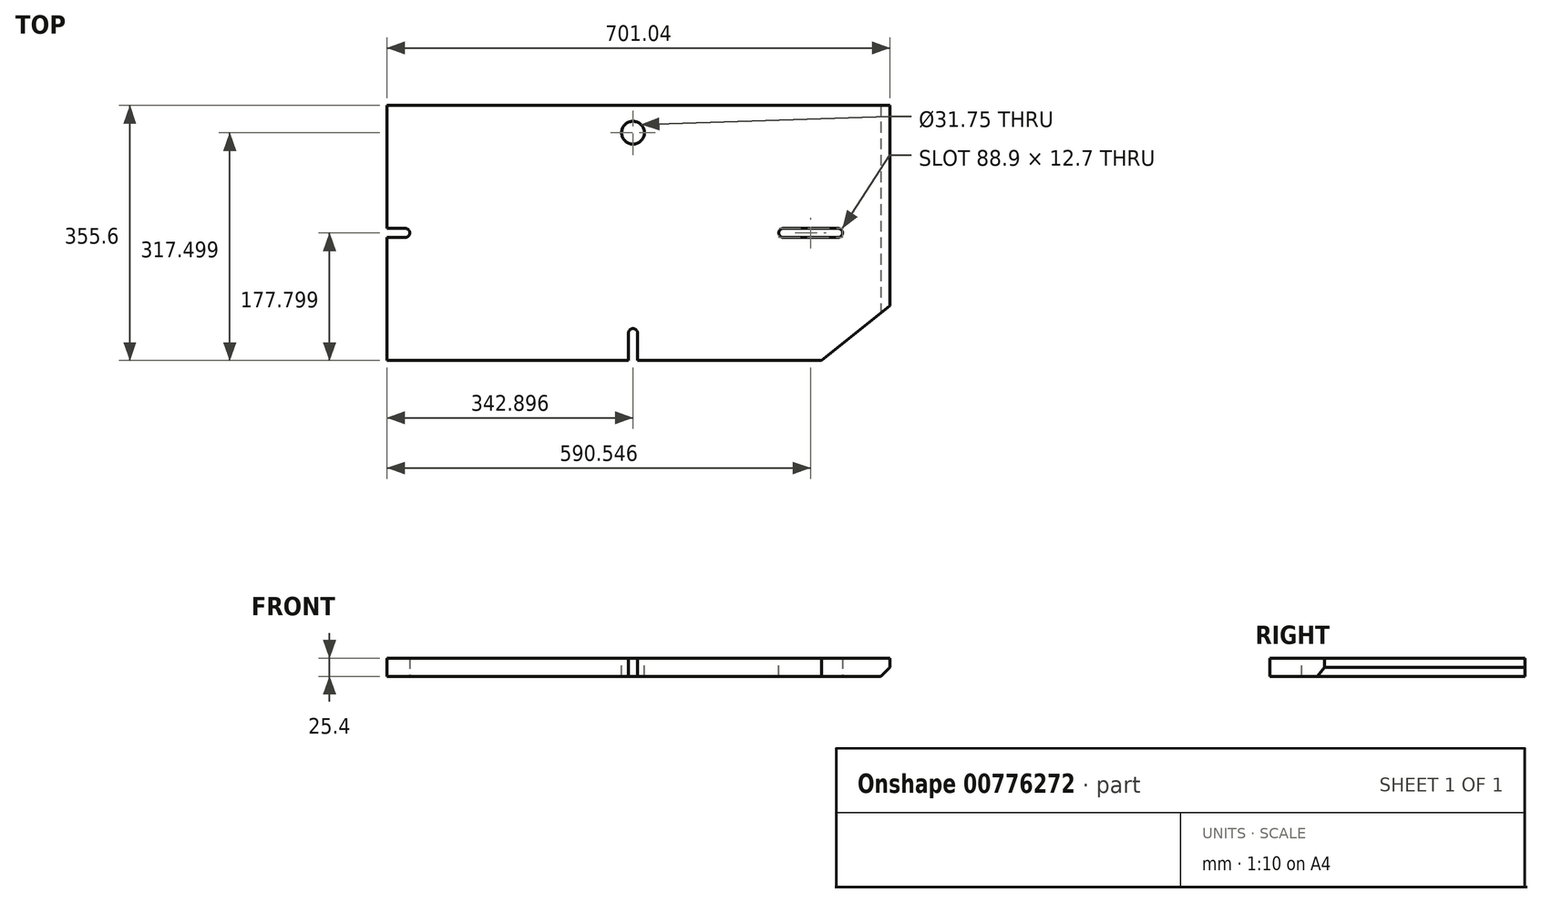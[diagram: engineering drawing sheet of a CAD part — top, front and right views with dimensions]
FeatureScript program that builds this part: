
annotation { "Feature Type Name" : "Feature", "Feature Type Description" : "" }
export const myFeature = defineFeature(function(context is Context, id is Id, definition is map)
    precondition{}
    {
        {
            var Q0;
            Q0=qCreatedBy(makeId("Top.planeOp"),FACE);
            var sketch = newSketch(context, id + "F0", { "sketchPlane" : qUnion([Q0])});
            skLineSegment(sketch, "E0.bottom", {"start": v(-409.1, 222.86) * mm, "end": v(-49.42, 222.86) * mm});
            skLineSegment(sketch, "E0.top", {"start": v(-409.1, -132.74) * mm, "end": v(196.69, -132.74) * mm});
            skLineSegment(sketch, "E0.left", {"start": v(-409.1, 222.86) * mm, "end": v(-409.1, 57.75) * mm});
            skLineSegment(sketch, "E0.right", {"start": v(291.94, 222.86) * mm, "end": v(291.94, -56.54) * mm});
            skLineSegment(sketch, "E1", {"start": v(196.69, -132.74) * mm, "end": v(291.94, -56.54) * mm});
            skLineSegment(sketch, "E2.trimOffspring", {"start": v(-409.1, 32.4) * mm, "end": v(-409.1, -132.74) * mm});
            skLineSegment(sketch, "E3.trimOffspring", {"start": v(-50.96, 222.86) * mm, "end": v(291.94, 222.86) * mm});
            skLineSegment(sketch, "E4", {"start": v(-409.1, 57.75) * mm, "end": v(-409.1, 32.4) * mm});
            skSolve(sketch);
        }
        {
            var Q0;
            Q0 = qSketchRegion(id + "F0", true);
            extrude(context, id + "F1", {"entities" : qUnion([Q0]), "depth" : 25.4 * mm, "offsetDistance" : 25.4 * mm});
        }
        {
            var Q0;
            Q0=makeQuery(id+"F1.opExtrude","CAP_FACE",FACE,{"disambiguationData":[OSD([sQuery(id+"F0.wireOp",EDGE,"E0.bottom"),sQuery(id+"F0.wireOp",EDGE,"E0.top"),sQuery(id+"F0.wireOp",EDGE,"E0.left"),sQuery(id+"F0.wireOp",EDGE,"E0.right"),sQuery(id+"F0.wireOp",EDGE,"E1"),sQuery(id+"F0.wireOp",EDGE,"E2.trimOffspring"),sQuery(id+"F0.wireOp",EDGE,"E3.trimOffspring"),sQuery(id+"F0.wireOp",EDGE,"E4")])],"isStart":false});
            var sketch = newSketch(context, id + "F2", { "sketchPlane" : qUnion([Q0])});
            skLineSegment(sketch, "E5.bottom", {"start": v(-409.1, 51.4) * mm, "end": v(-377.35, 51.4) * mm});
            skLineSegment(sketch, "E5.top", {"start": v(-409.1, 38.7) * mm, "end": v(-377.35, 38.7) * mm});
            skLineSegment(sketch, "E5.left", {"start": v(-409.1, 51.4) * mm, "end": v(-409.1, 38.7) * mm});
            skLineSegment(sketch, "E5.right", {"start": v(-377.35, 51.4) * mm, "end": v(-377.35, 38.7) * mm});
            skLineSegment(sketch, "E6.bottom", {"start": v(137, 51.4) * mm, "end": v(225.9, 51.4) * mm});
            skLineSegment(sketch, "E6.top", {"start": v(137, 38.7) * mm, "end": v(225.9, 38.7) * mm});
            skLineSegment(sketch, "E6.left", {"start": v(137, 51.4) * mm, "end": v(137, 38.7) * mm});
            skLineSegment(sketch, "E6.right", {"start": v(225.9, 51.4) * mm, "end": v(225.9, 38.7) * mm});
            skArc(sketch, "E7", {"start": v(-59.85, -94.64) * mm, "mid": v(-66.2, -88.3) * mm, "end": v(-72.55, -94.64) * mm});
            skLineSegment(sketch, "E8", {"start": v(-72.55, -94.64) * mm, "end": v(-72.55, -137.45) * mm});
            skLineSegment(sketch, "E9", {"start": v(-59.85, -94.64) * mm, "end": v(-59.85, -142.53) * mm});
            skLineSegment(sketch, "E10", {"start": v(-72.55, -137.45) * mm, "end": v(-59.85, -142.53) * mm});
            skCircle(sketch, "E11", {"center": v(-66.2, 184.76) * mm, "radius": 15.88 * mm});
            skSolve(sketch);
        }
        {
            var Q0;
            Q0 = qSketchRegion(id + "F2", true);
            extrude(context, id + "F3", {"entities" : qUnion([Q0]), "operationType" : NewBodyOperationType.REMOVE, "endBound" : BoundingType.THROUGH_ALL, "oppositeDirection" : true, "depth" : 25.4 * mm, "offsetDistance" : 25.4 * mm});
        }
        {
            var Q0;
            Q0=makeQuery(id+"F3.boolean.opBoolean","COPY",EDGE,{"derivedFrom":makeQuery(id+"F3.opExtrude","SWEPT_EDGE",EDGE,{"disambiguationData":[OSD([sQuery(id+"F2.wireOp",EDGE,"E5.bottom"),sQuery(id+"F2.wireOp",EDGE,"E5.right")])]})});
            var Q1;
            Q1=makeQuery(id+"F3.boolean.opBoolean","COPY",EDGE,{"derivedFrom":makeQuery(id+"F3.opExtrude","SWEPT_EDGE",EDGE,{"disambiguationData":[OSD([sQuery(id+"F2.wireOp",EDGE,"E6.bottom"),sQuery(id+"F2.wireOp",EDGE,"E6.right")])]})});
            var Q2;
            Q2=makeQuery(id+"F3.boolean.opBoolean","COPY",EDGE,{"derivedFrom":makeQuery(id+"F3.opExtrude","SWEPT_EDGE",EDGE,{"disambiguationData":[OSD([sQuery(id+"F2.wireOp",EDGE,"E6.top"),sQuery(id+"F2.wireOp",EDGE,"E6.right")])]})});
            var Q3;
            Q3=makeQuery(id+"F3.boolean.opBoolean","COPY",EDGE,{"derivedFrom":makeQuery(id+"F3.opExtrude","SWEPT_EDGE",EDGE,{"disambiguationData":[OSD([sQuery(id+"F2.wireOp",EDGE,"E5.top"),sQuery(id+"F2.wireOp",EDGE,"E5.right")])]})});
            var Q4;
            Q4=makeQuery(id+"F3.boolean.opBoolean","COPY",EDGE,{"derivedFrom":makeQuery(id+"F3.opExtrude","SWEPT_EDGE",EDGE,{"disambiguationData":[OSD([sQuery(id+"F2.wireOp",EDGE,"E6.bottom"),sQuery(id+"F2.wireOp",EDGE,"E6.left")])]})});
            var Q5;
            Q5=makeQuery(id+"F3.boolean.opBoolean","COPY",EDGE,{"derivedFrom":makeQuery(id+"F3.opExtrude","SWEPT_EDGE",EDGE,{"disambiguationData":[OSD([sQuery(id+"F2.wireOp",EDGE,"E6.top"),sQuery(id+"F2.wireOp",EDGE,"E6.left")])]})});
            fillet(context, id + "F4", {"entities" : qUnion([Q0, Q1, Q2, Q3, Q4, Q5]), "radius" : 6.35 * mm, "tangentPropagation" : true, "allowEdgeOverflow" : false});
        }
        {
            var Q0;
            Q0=makeQuery(id+"F1.opExtrude","CAP_EDGE",EDGE,{"disambiguationData":[OSD([sQuery(id+"F0.wireOp",EDGE,"E0.right")])],"isStart":true});
            chamfer(context, id + "F5", {"entities" : qUnion([Q0]), "width" : 12.7 * mm, "tangentPropagation" : true});
        }
    });
